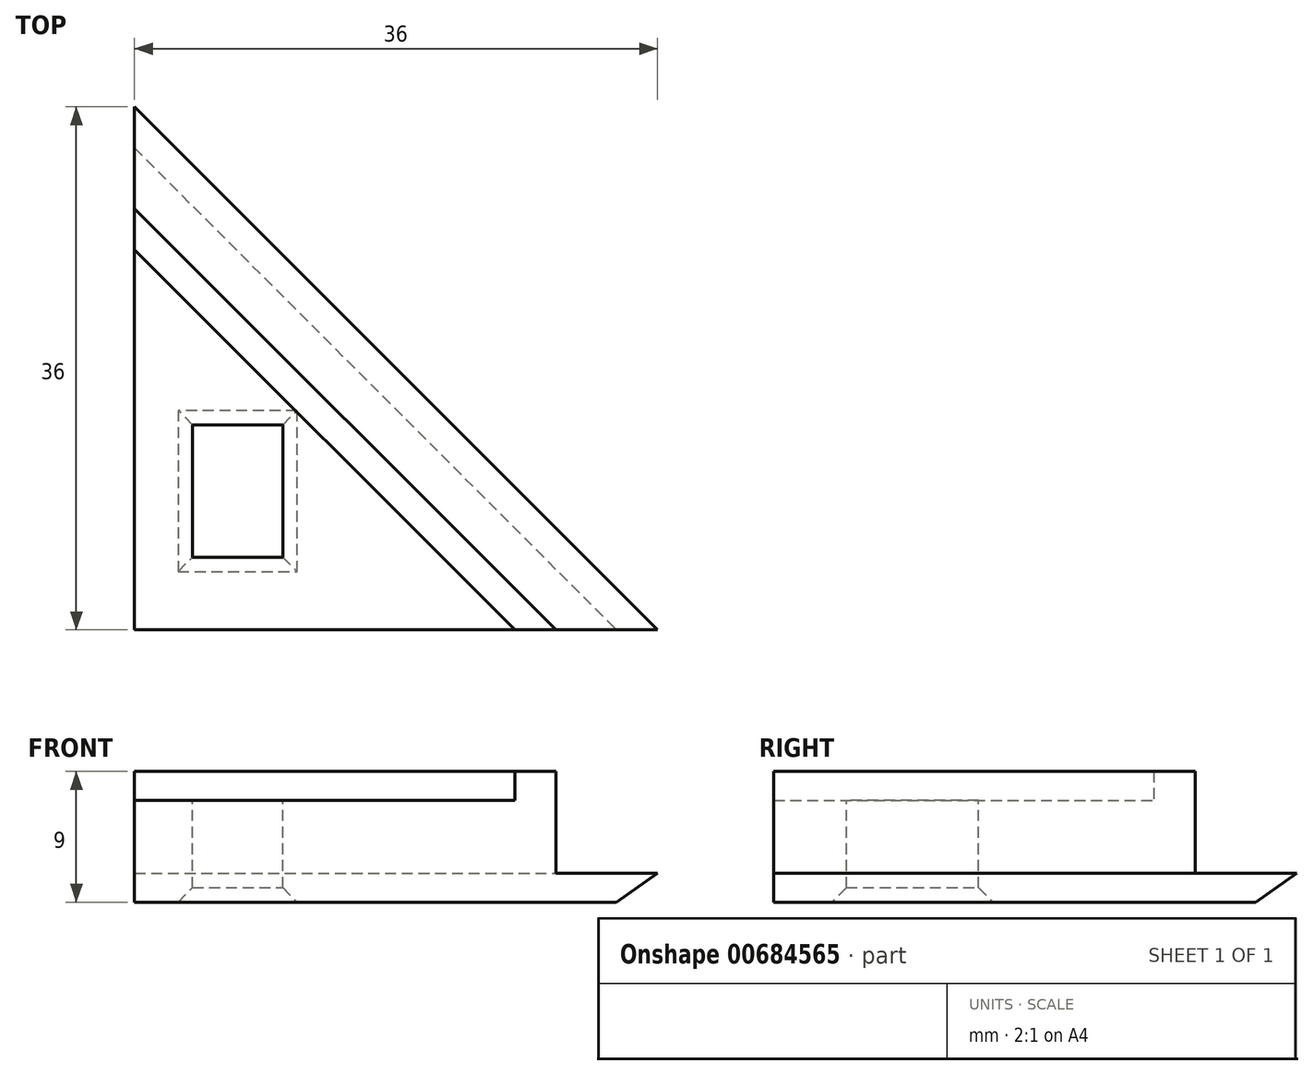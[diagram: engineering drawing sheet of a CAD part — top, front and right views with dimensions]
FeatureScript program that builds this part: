
annotation { "Feature Type Name" : "Feature", "Feature Type Description" : "" }
export const myFeature = defineFeature(function(context is Context, id is Id, definition is map)
    precondition{}
    {
        {
            var Q0;
            Q0=qCreatedBy(makeId("Top.planeOp"),FACE);
            var sketch = newSketch(context, id + "F0", { "sketchPlane" : qUnion([Q0])});
            skLineSegment(sketch, "E0", {"start": v(0, 0) * mm, "end": v(0, 36) * mm});
            skLineSegment(sketch, "E1", {"start": v(0, 36) * mm, "end": v(36, 0) * mm});
            skLineSegment(sketch, "E2", {"start": v(36, 0) * mm, "end": v(0, 0) * mm});
            skSolve(sketch);
        }
        {
            var Q0;
            Q0=makeQuery(id+"F0.imprint","IMPRINT",FACE,{"disambiguationData":[TD([[makeQuery(id+"F0.imprint","IMPRINT",EDGE,{"derivedFrom":sQuery(id+"F0.wireOp",EDGE,"E0")}),-1.0]])]});
            extrude(context, id + "F1", {"entities" : qUnion([Q0]), "depth" : 2 * mm});
        }
        {
            var Q0;
            Q0=makeQuery(id+"F1.opExtrude","CAP_FACE",FACE,{"disambiguationData":[OSD([sQuery(id+"F0.wireOp",EDGE,"E0"),sQuery(id+"F0.wireOp",EDGE,"E1"),sQuery(id+"F0.wireOp",EDGE,"E2")])],"isStart":false});
            var sketch = newSketch(context, id + "F2", { "sketchPlane" : qUnion([Q0])});
            skLineSegment(sketch, "E3", {"start": v(0, 0) * mm, "end": v(0, 29) * mm});
            skLineSegment(sketch, "E4", {"start": v(0, 29) * mm, "end": v(29, 0) * mm});
            skLineSegment(sketch, "E5", {"start": v(29, 0) * mm, "end": v(0, 0) * mm});
            skSolve(sketch);
        }
        {
            var Q0;
            Q0=makeQuery(id+"F2.imprint","IMPRINT",FACE,{"disambiguationData":[TD([[makeQuery(id+"F2.imprint","IMPRINT",EDGE,{"derivedFrom":sQuery(id+"F2.wireOp",EDGE,"E3")}),-1.0]])]});
            extrude(context, id + "F3", {"entities" : qUnion([Q0]), "operationType" : NewBodyOperationType.ADD, "depth" : 5 * mm});
        }
        {
            var Q0;
            Q0=makeQuery(id+"F3.opExtrude","CAP_FACE",FACE,{"disambiguationData":[OSD([sQuery(id+"F2.wireOp",EDGE,"E3"),sQuery(id+"F2.wireOp",EDGE,"E4"),sQuery(id+"F2.wireOp",EDGE,"E5")])],"isStart":false});
            var sketch = newSketch(context, id + "F4", { "sketchPlane" : qUnion([Q0])});
            skLineSegment(sketch, "E6", {"start": v(0, 29) * mm, "end": v(29, 0) * mm});
            skLineSegment(sketch, "E7", {"start": v(29, 0) * mm, "end": v(26.17, 0) * mm});
            skLineSegment(sketch, "E8", {"start": v(26.17, 0) * mm, "end": v(0, 26.17) * mm});
            skLineSegment(sketch, "E9", {"start": v(0, 26.17) * mm, "end": v(0, 29) * mm});
            skSolve(sketch);
        }
        {
            var Q0;
            Q0=makeQuery(id+"F4.imprint","IMPRINT",FACE,{"disambiguationData":[TD([[makeQuery(id+"F4.imprint","IMPRINT",EDGE,{"derivedFrom":sQuery(id+"F4.wireOp",EDGE,"E6")}),-1.0]])]});
            extrude(context, id + "F5", {"entities" : qUnion([Q0]), "operationType" : NewBodyOperationType.ADD, "depth" : 2 * mm});
        }
        {
            var Q0;
            Q0=makeQuery(id+"F3.opExtrude","CAP_FACE",FACE,{"disambiguationData":[OSD([sQuery(id+"F2.wireOp",EDGE,"E3"),sQuery(id+"F2.wireOp",EDGE,"E4"),sQuery(id+"F2.wireOp",EDGE,"E5")])],"isStart":false});
            var sketch = newSketch(context, id + "F6", { "sketchPlane" : qUnion([Q0])});
            skLineSegment(sketch, "E10.bottom", {"start": v(4, 14.1) * mm, "end": v(10.2, 14.1) * mm});
            skLineSegment(sketch, "E10.top", {"start": v(4, 5) * mm, "end": v(10.2, 5) * mm});
            skLineSegment(sketch, "E10.left", {"start": v(4, 14.1) * mm, "end": v(4, 5) * mm});
            skLineSegment(sketch, "E10.right", {"start": v(10.2, 14.1) * mm, "end": v(10.2, 5) * mm});
            skSolve(sketch);
        }
        {
            var Q0;
            Q0=makeQuery(id+"F6.imprint","IMPRINT",FACE,{"disambiguationData":[TD([[makeQuery(id+"F6.imprint","IMPRINT",EDGE,{"derivedFrom":sQuery(id+"F6.wireOp",EDGE,"E10.bottom")}),-1.0]])]});
            extrude(context, id + "F7", {"entities" : qUnion([Q0]), "operationType" : NewBodyOperationType.REMOVE, "endBound" : BoundingType.THROUGH_ALL, "oppositeDirection" : true, "depth" : 25 * mm});
        }
        {
            var Q0;
            Q0=makeQuery(id+"F7.boolean.opBoolean","COPY",EDGE,{"derivedFrom":makeQuery(id+"F7.opExtrude","CAP_EDGE",EDGE,{"disambiguationData":[OSD([sQuery(id+"F6.wireOp",EDGE,"E10.left")])],"isStart":true})});
            var Q1;
            Q1=makeQuery(id+"F7.boolean.opBoolean","COPY",EDGE,{"derivedFrom":makeQuery(id+"F7.opExtrude","CAP_EDGE",EDGE,{"disambiguationData":[OSD([sQuery(id+"F6.wireOp",EDGE,"E10.bottom")])],"isStart":true})});
            var Q2;
            Q2=makeQuery(id+"F7.boolean.opBoolean","COPY",EDGE,{"derivedFrom":makeQuery(id+"F7.opExtrude","CAP_EDGE",EDGE,{"disambiguationData":[OSD([sQuery(id+"F6.wireOp",EDGE,"E10.right")])],"isStart":true})});
            var Q3;
            Q3=makeQuery(id+"F7.boolean.opBoolean","COPY",EDGE,{"derivedFrom":makeQuery(id+"F7.opExtrude","CAP_EDGE",EDGE,{"disambiguationData":[OSD([sQuery(id+"F6.wireOp",EDGE,"E10.top")])],"isStart":true})});
            var Q4;
            Q4=makeQuery(id+"F7.boolean.opBoolean","INTERSECT",EDGE,{"derivedFrom":[makeQuery(id+"F1.opExtrude","CAP_FACE",FACE,{"disambiguationData":[OSD([sQuery(id+"F0.wireOp",EDGE,"E0"),sQuery(id+"F0.wireOp",EDGE,"E1"),sQuery(id+"F0.wireOp",EDGE,"E2")])],"isStart":true}),makeQuery(id+"F7.opExtrude","SWEPT_FACE",FACE,{"disambiguationData":[OSD([sQuery(id+"F6.wireOp",EDGE,"E10.bottom")])]})]});
            var Q5;
            Q5=makeQuery(id+"F7.boolean.opBoolean","INTERSECT",EDGE,{"derivedFrom":[makeQuery(id+"F1.opExtrude","CAP_FACE",FACE,{"disambiguationData":[OSD([sQuery(id+"F0.wireOp",EDGE,"E0"),sQuery(id+"F0.wireOp",EDGE,"E1"),sQuery(id+"F0.wireOp",EDGE,"E2")])],"isStart":true}),makeQuery(id+"F7.opExtrude","SWEPT_FACE",FACE,{"disambiguationData":[OSD([sQuery(id+"F6.wireOp",EDGE,"E10.right")])]})]});
            var Q6;
            Q6=makeQuery(id+"F7.boolean.opBoolean","INTERSECT",EDGE,{"derivedFrom":[makeQuery(id+"F1.opExtrude","CAP_FACE",FACE,{"disambiguationData":[OSD([sQuery(id+"F0.wireOp",EDGE,"E0"),sQuery(id+"F0.wireOp",EDGE,"E1"),sQuery(id+"F0.wireOp",EDGE,"E2")])],"isStart":true}),makeQuery(id+"F7.opExtrude","SWEPT_FACE",FACE,{"disambiguationData":[OSD([sQuery(id+"F6.wireOp",EDGE,"E10.top")])]})]});
            var Q7;
            Q7=makeQuery(id+"F7.boolean.opBoolean","INTERSECT",EDGE,{"derivedFrom":[makeQuery(id+"F1.opExtrude","CAP_FACE",FACE,{"disambiguationData":[OSD([sQuery(id+"F0.wireOp",EDGE,"E0"),sQuery(id+"F0.wireOp",EDGE,"E1"),sQuery(id+"F0.wireOp",EDGE,"E2")])],"isStart":true}),makeQuery(id+"F7.opExtrude","SWEPT_FACE",FACE,{"disambiguationData":[OSD([sQuery(id+"F6.wireOp",EDGE,"E10.left")])]})]});
            chamfer(context, id + "F8", {"entities" : qUnion([Q0, Q1, Q2, Q3, Q4, Q5, Q6, Q7]), "width" : 1 * mm, "tangentPropagation" : true});
        }
        {
            var Q0;
            Q0=makeQuery(id+"F1.opExtrude","CAP_EDGE",EDGE,{"disambiguationData":[OSD([sQuery(id+"F0.wireOp",EDGE,"E1")])],"isStart":true});
            chamfer(context, id + "F9", {"entities" : qUnion([Q0]), "width" : 2 * mm, "tangentPropagation" : true});
        }
    });
